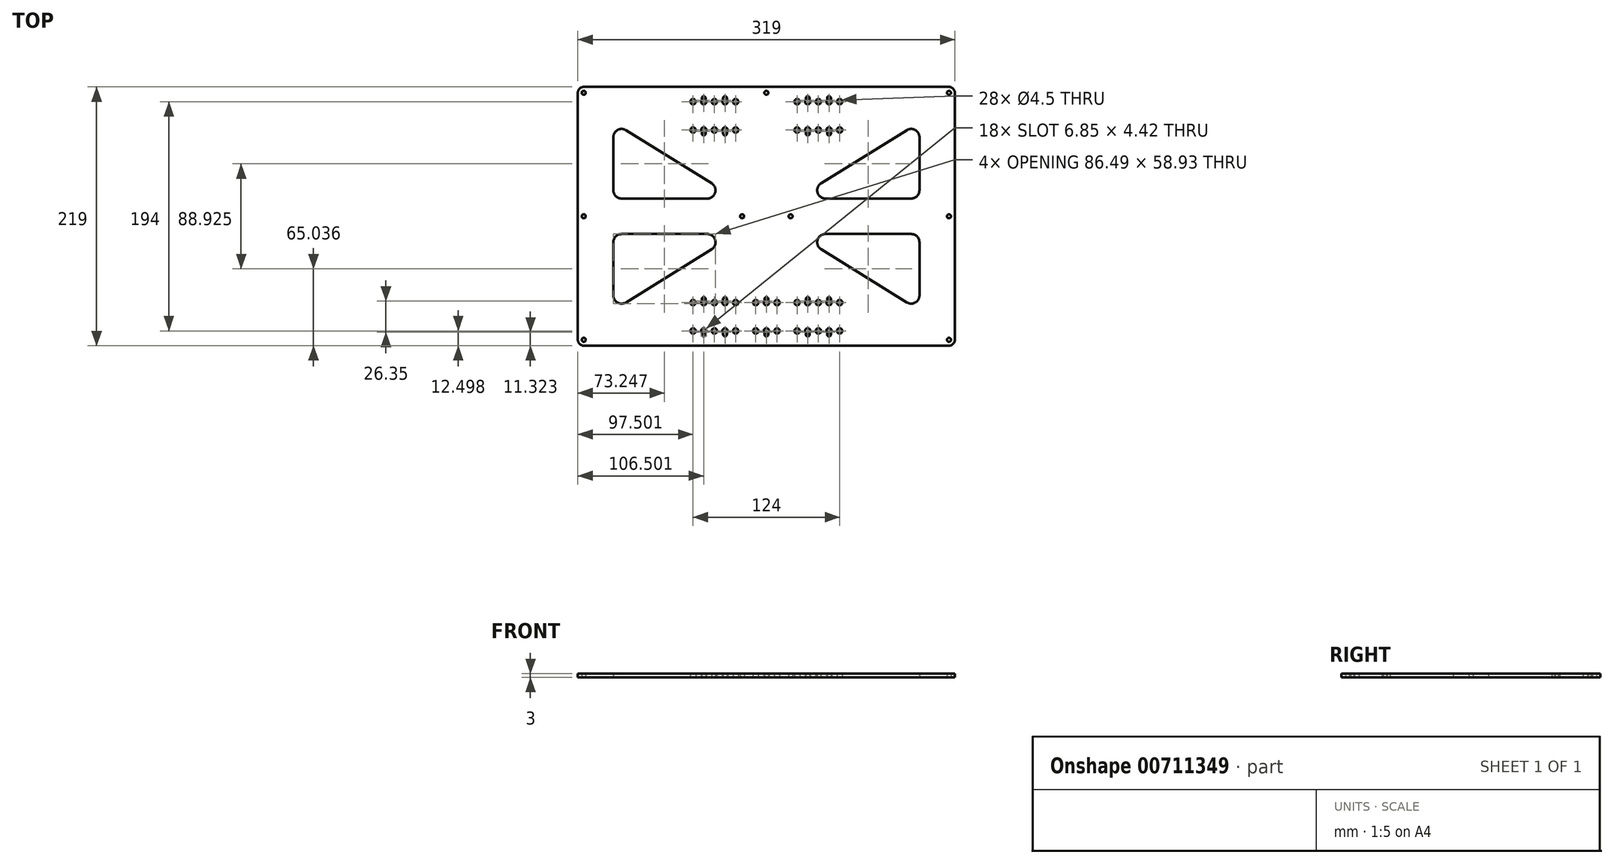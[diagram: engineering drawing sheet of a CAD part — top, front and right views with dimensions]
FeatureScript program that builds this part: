
annotation { "Feature Type Name" : "Feature", "Feature Type Description" : "" }
export const myFeature = defineFeature(function(context is Context, id is Id, definition is map)
    precondition{}
    {
        {
            var Q0;
            Q0=qCreatedBy(makeId("Top.planeOp"),FACE);
            var sketch = newSketch(context, id + "F0", { "sketchPlane" : qUnion([Q0])});
            skLineSegment(sketch, "E0", {"start": v(276.47, 208.94) * mm, "end": v(276.47, 207.52) * mm});
            skArc(sketch, "E1", {"start": v(276.47, 208.94) * mm, "mid": v(274.87, 212.77) * mm, "end": v(273.27, 208.94) * mm});
            skLineSegment(sketch, "E2", {"start": v(273.27, 207.52) * mm, "end": v(273.27, 208.94) * mm});
            skArc(sketch, "E3", {"start": v(273.27, 207.52) * mm, "mid": v(274.87, 205.92) * mm, "end": v(276.47, 207.52) * mm});
            skLineSegment(sketch, "E4", {"start": v(273.27, 236.1) * mm, "end": v(273.27, 237.52) * mm});
            skArc(sketch, "E5", {"start": v(273.27, 236.1) * mm, "mid": v(274.87, 232.27) * mm, "end": v(276.47, 236.1) * mm});
            skLineSegment(sketch, "E6", {"start": v(276.47, 237.52) * mm, "end": v(276.47, 236.1) * mm});
            skArc(sketch, "E7", {"start": v(276.47, 237.52) * mm, "mid": v(274.87, 239.12) * mm, "end": v(273.27, 237.52) * mm});
            skLineSegment(sketch, "E8", {"start": v(170.47, 208.94) * mm, "end": v(170.47, 207.52) * mm});
            skArc(sketch, "E9", {"start": v(170.47, 208.94) * mm, "mid": v(168.87, 212.77) * mm, "end": v(167.27, 208.94) * mm});
            skLineSegment(sketch, "E10", {"start": v(167.27, 207.52) * mm, "end": v(167.27, 208.94) * mm});
            skArc(sketch, "E11", {"start": v(167.27, 207.52) * mm, "mid": v(168.87, 205.92) * mm, "end": v(170.47, 207.52) * mm});
            skLineSegment(sketch, "E12", {"start": v(167.27, 236.1) * mm, "end": v(167.27, 237.52) * mm});
            skArc(sketch, "E13", {"start": v(167.27, 236.1) * mm, "mid": v(168.87, 232.27) * mm, "end": v(170.47, 236.1) * mm});
            skLineSegment(sketch, "E14", {"start": v(170.47, 237.52) * mm, "end": v(170.47, 236.1) * mm});
            skArc(sketch, "E15", {"start": v(170.47, 237.52) * mm, "mid": v(168.87, 239.12) * mm, "end": v(167.27, 237.52) * mm});
            skLineSegment(sketch, "E16", {"start": v(258.47, 208.94) * mm, "end": v(258.47, 207.52) * mm});
            skArc(sketch, "E17", {"start": v(258.47, 208.94) * mm, "mid": v(256.87, 212.77) * mm, "end": v(255.27, 208.94) * mm});
            skLineSegment(sketch, "E18", {"start": v(255.27, 207.52) * mm, "end": v(255.27, 208.94) * mm});
            skArc(sketch, "E19", {"start": v(255.27, 207.52) * mm, "mid": v(256.87, 205.92) * mm, "end": v(258.47, 207.52) * mm});
            skLineSegment(sketch, "E20", {"start": v(255.27, 236.1) * mm, "end": v(255.27, 237.52) * mm});
            skArc(sketch, "E21", {"start": v(255.27, 236.1) * mm, "mid": v(256.87, 232.27) * mm, "end": v(258.47, 236.1) * mm});
            skLineSegment(sketch, "E22", {"start": v(258.47, 237.52) * mm, "end": v(258.47, 236.1) * mm});
            skArc(sketch, "E23", {"start": v(258.47, 237.52) * mm, "mid": v(256.87, 239.12) * mm, "end": v(255.27, 237.52) * mm});
            skLineSegment(sketch, "E24", {"start": v(188.47, 208.94) * mm, "end": v(188.47, 207.52) * mm});
            skArc(sketch, "E25", {"start": v(188.47, 208.94) * mm, "mid": v(186.87, 212.77) * mm, "end": v(185.27, 208.94) * mm});
            skLineSegment(sketch, "E26", {"start": v(185.27, 207.52) * mm, "end": v(185.27, 208.94) * mm});
            skArc(sketch, "E27", {"start": v(185.27, 207.52) * mm, "mid": v(186.87, 205.92) * mm, "end": v(188.47, 207.52) * mm});
            skLineSegment(sketch, "E28", {"start": v(185.27, 236.1) * mm, "end": v(185.27, 237.52) * mm});
            skArc(sketch, "E29", {"start": v(185.27, 236.1) * mm, "mid": v(186.87, 232.27) * mm, "end": v(188.47, 236.1) * mm});
            skLineSegment(sketch, "E30", {"start": v(188.47, 237.52) * mm, "end": v(188.47, 236.1) * mm});
            skArc(sketch, "E31", {"start": v(188.47, 237.52) * mm, "mid": v(186.87, 239.12) * mm, "end": v(185.27, 237.52) * mm});
            skArc(sketch, "E32", {"start": v(62.37, 33.02) * mm, "mid": v(63.84, 29.48) * mm, "end": v(67.37, 28.02) * mm});
            skLineSegment(sketch, "E33", {"start": v(62.37, 242.02) * mm, "end": v(62.37, 33.02) * mm});
            skArc(sketch, "E34", {"start": v(67.37, 247.02) * mm, "mid": v(63.84, 245.55) * mm, "end": v(62.37, 242.02) * mm});
            skLineSegment(sketch, "E35", {"start": v(376.37, 247.02) * mm, "end": v(67.37, 247.02) * mm});
            skArc(sketch, "E36", {"start": v(381.37, 242.02) * mm, "mid": v(379.9, 245.55) * mm, "end": v(376.37, 247.02) * mm});
            skLineSegment(sketch, "E37", {"start": v(381.37, 33.02) * mm, "end": v(381.37, 242.02) * mm});
            skArc(sketch, "E38", {"start": v(376.37, 28.02) * mm, "mid": v(379.9, 29.48) * mm, "end": v(381.37, 33.02) * mm});
            skLineSegment(sketch, "E39", {"start": v(67.37, 28.02) * mm, "end": v(376.37, 28.02) * mm});
            skCircle(sketch, "E40", {"center": v(221.87, 242.02) * mm, "radius": 1.7 * mm});
            skCircle(sketch, "E41", {"center": v(376.37, 242.02) * mm, "radius": 1.7 * mm});
            skCircle(sketch, "E42", {"center": v(376.37, 137.52) * mm, "radius": 1.7 * mm});
            skCircle(sketch, "E43", {"center": v(67.37, 242.02) * mm, "radius": 1.7 * mm});
            skCircle(sketch, "E44", {"center": v(67.37, 137.52) * mm, "radius": 1.7 * mm});
            skCircle(sketch, "E45", {"center": v(67.37, 33.02) * mm, "radius": 1.7 * mm});
            skCircle(sketch, "E46", {"center": v(230.87, 40.52) * mm, "radius": 2.25 * mm});
            skCircle(sketch, "E47", {"center": v(230.87, 64.52) * mm, "radius": 2.25 * mm});
            skCircle(sketch, "E48", {"center": v(212.87, 64.52) * mm, "radius": 2.25 * mm});
            skCircle(sketch, "E49", {"center": v(212.87, 40.52) * mm, "radius": 2.25 * mm});
            skArc(sketch, "E50", {"start": v(220.27, 37.52) * mm, "mid": v(221.87, 35.92) * mm, "end": v(223.47, 37.52) * mm});
            skLineSegment(sketch, "E51", {"start": v(223.47, 37.52) * mm, "end": v(223.47, 38.94) * mm});
            skArc(sketch, "E52", {"start": v(223.47, 38.94) * mm, "mid": v(221.87, 42.77) * mm, "end": v(220.27, 38.94) * mm});
            skLineSegment(sketch, "E53", {"start": v(220.27, 38.94) * mm, "end": v(220.27, 37.52) * mm});
            skArc(sketch, "E54", {"start": v(223.47, 67.52) * mm, "mid": v(221.87, 69.12) * mm, "end": v(220.27, 67.52) * mm});
            skLineSegment(sketch, "E55", {"start": v(220.27, 67.52) * mm, "end": v(220.27, 66.1) * mm});
            skArc(sketch, "E56", {"start": v(220.27, 66.1) * mm, "mid": v(221.87, 62.27) * mm, "end": v(223.47, 66.1) * mm});
            skLineSegment(sketch, "E57", {"start": v(223.47, 66.1) * mm, "end": v(223.47, 67.52) * mm});
            skCircle(sketch, "E58", {"center": v(195.87, 40.52) * mm, "radius": 2.25 * mm});
            skCircle(sketch, "E59", {"center": v(195.87, 64.52) * mm, "radius": 2.25 * mm});
            skCircle(sketch, "E60", {"center": v(177.87, 64.52) * mm, "radius": 2.25 * mm});
            skCircle(sketch, "E61", {"center": v(177.87, 40.52) * mm, "radius": 2.25 * mm});
            skCircle(sketch, "E62", {"center": v(265.87, 40.52) * mm, "radius": 2.25 * mm});
            skCircle(sketch, "E63", {"center": v(265.87, 64.52) * mm, "radius": 2.25 * mm});
            skCircle(sketch, "E64", {"center": v(247.87, 64.52) * mm, "radius": 2.25 * mm});
            skCircle(sketch, "E65", {"center": v(247.87, 40.52) * mm, "radius": 2.25 * mm});
            skCircle(sketch, "E66", {"center": v(159.87, 64.52) * mm, "radius": 2.25 * mm});
            skCircle(sketch, "E67", {"center": v(159.87, 40.52) * mm, "radius": 2.25 * mm});
            skCircle(sketch, "E68", {"center": v(283.87, 40.52) * mm, "radius": 2.25 * mm});
            skCircle(sketch, "E69", {"center": v(283.87, 64.52) * mm, "radius": 2.25 * mm});
            skArc(sketch, "E70", {"start": v(185.27, 37.52) * mm, "mid": v(186.87, 35.92) * mm, "end": v(188.47, 37.52) * mm});
            skLineSegment(sketch, "E71", {"start": v(188.47, 37.52) * mm, "end": v(188.47, 38.94) * mm});
            skArc(sketch, "E72", {"start": v(188.47, 38.94) * mm, "mid": v(186.87, 42.77) * mm, "end": v(185.27, 38.94) * mm});
            skLineSegment(sketch, "E73", {"start": v(185.27, 38.94) * mm, "end": v(185.27, 37.52) * mm});
            skArc(sketch, "E74", {"start": v(188.47, 67.52) * mm, "mid": v(186.87, 69.12) * mm, "end": v(185.27, 67.52) * mm});
            skLineSegment(sketch, "E75", {"start": v(185.27, 67.52) * mm, "end": v(185.27, 66.1) * mm});
            skArc(sketch, "E76", {"start": v(185.27, 66.1) * mm, "mid": v(186.87, 62.27) * mm, "end": v(188.47, 66.1) * mm});
            skLineSegment(sketch, "E77", {"start": v(188.47, 66.1) * mm, "end": v(188.47, 67.52) * mm});
            skArc(sketch, "E78", {"start": v(255.27, 37.52) * mm, "mid": v(256.87, 35.92) * mm, "end": v(258.47, 37.52) * mm});
            skLineSegment(sketch, "E79", {"start": v(258.47, 37.52) * mm, "end": v(258.47, 38.94) * mm});
            skArc(sketch, "E80", {"start": v(258.47, 38.94) * mm, "mid": v(256.87, 42.77) * mm, "end": v(255.27, 38.94) * mm});
            skLineSegment(sketch, "E81", {"start": v(255.27, 38.94) * mm, "end": v(255.27, 37.52) * mm});
            skArc(sketch, "E82", {"start": v(258.47, 67.52) * mm, "mid": v(256.87, 69.12) * mm, "end": v(255.27, 67.52) * mm});
            skLineSegment(sketch, "E83", {"start": v(255.27, 67.52) * mm, "end": v(255.27, 66.1) * mm});
            skArc(sketch, "E84", {"start": v(255.27, 66.1) * mm, "mid": v(256.87, 62.27) * mm, "end": v(258.47, 66.1) * mm});
            skLineSegment(sketch, "E85", {"start": v(258.47, 66.1) * mm, "end": v(258.47, 67.52) * mm});
            skArc(sketch, "E86", {"start": v(167.27, 37.52) * mm, "mid": v(168.87, 35.92) * mm, "end": v(170.47, 37.52) * mm});
            skLineSegment(sketch, "E87", {"start": v(170.47, 37.52) * mm, "end": v(170.47, 38.94) * mm});
            skArc(sketch, "E88", {"start": v(170.47, 38.94) * mm, "mid": v(168.87, 42.77) * mm, "end": v(167.27, 38.94) * mm});
            skLineSegment(sketch, "E89", {"start": v(167.27, 38.94) * mm, "end": v(167.27, 37.52) * mm});
            skArc(sketch, "E90", {"start": v(170.47, 67.52) * mm, "mid": v(168.87, 69.12) * mm, "end": v(167.27, 67.52) * mm});
            skLineSegment(sketch, "E91", {"start": v(167.27, 67.52) * mm, "end": v(167.27, 66.1) * mm});
            skArc(sketch, "E92", {"start": v(167.27, 66.1) * mm, "mid": v(168.87, 62.27) * mm, "end": v(170.47, 66.1) * mm});
            skLineSegment(sketch, "E93", {"start": v(170.47, 66.1) * mm, "end": v(170.47, 67.52) * mm});
            skArc(sketch, "E94", {"start": v(273.27, 37.52) * mm, "mid": v(274.87, 35.92) * mm, "end": v(276.47, 37.52) * mm});
            skLineSegment(sketch, "E95", {"start": v(276.47, 37.52) * mm, "end": v(276.47, 38.94) * mm});
            skArc(sketch, "E96", {"start": v(276.47, 38.94) * mm, "mid": v(274.87, 42.77) * mm, "end": v(273.27, 38.94) * mm});
            skLineSegment(sketch, "E97", {"start": v(273.27, 38.94) * mm, "end": v(273.27, 37.52) * mm});
            skArc(sketch, "E98", {"start": v(276.47, 67.52) * mm, "mid": v(274.87, 69.12) * mm, "end": v(273.27, 67.52) * mm});
            skLineSegment(sketch, "E99", {"start": v(273.27, 67.52) * mm, "end": v(273.27, 66.1) * mm});
            skArc(sketch, "E100", {"start": v(273.27, 66.1) * mm, "mid": v(274.87, 62.27) * mm, "end": v(276.47, 66.1) * mm});
            skLineSegment(sketch, "E101", {"start": v(276.47, 66.1) * mm, "end": v(276.47, 67.52) * mm});
            skLineSegment(sketch, "E102", {"start": v(171.87, 122.52) * mm, "end": v(99.37, 122.52) * mm});
            skArc(sketch, "E103", {"start": v(99.37, 122.52) * mm, "mid": v(94.42, 120.47) * mm, "end": v(92.37, 115.52) * mm});
            skLineSegment(sketch, "E104", {"start": v(92.37, 115.52) * mm, "end": v(92.37, 70.6) * mm});
            skArc(sketch, "E105", {"start": v(92.37, 70.6) * mm, "mid": v(95.97, 64.48) * mm, "end": v(103.06, 64.64) * mm});
            skLineSegment(sketch, "E106", {"start": v(103.06, 64.64) * mm, "end": v(175.56, 109.57) * mm});
            skArc(sketch, "E107", {"start": v(175.56, 109.57) * mm, "mid": v(178.6, 117.44) * mm, "end": v(171.87, 122.52) * mm});
            skLineSegment(sketch, "E108", {"start": v(92.37, 204.45) * mm, "end": v(92.37, 159.52) * mm});
            skArc(sketch, "E109", {"start": v(92.37, 159.52) * mm, "mid": v(94.42, 154.57) * mm, "end": v(99.37, 152.52) * mm});
            skLineSegment(sketch, "E110", {"start": v(99.37, 152.52) * mm, "end": v(171.87, 152.52) * mm});
            skArc(sketch, "E111", {"start": v(171.87, 152.52) * mm, "mid": v(178.6, 157.6) * mm, "end": v(175.56, 165.47) * mm});
            skLineSegment(sketch, "E112", {"start": v(175.56, 165.47) * mm, "end": v(103.06, 210.4) * mm});
            skArc(sketch, "E113", {"start": v(103.06, 210.4) * mm, "mid": v(95.97, 210.56) * mm, "end": v(92.37, 204.45) * mm});
            skLineSegment(sketch, "E114", {"start": v(271.87, 152.52) * mm, "end": v(344.37, 152.52) * mm});
            skArc(sketch, "E115", {"start": v(344.37, 152.52) * mm, "mid": v(349.32, 154.57) * mm, "end": v(351.37, 159.52) * mm});
            skLineSegment(sketch, "E116", {"start": v(351.37, 159.52) * mm, "end": v(351.37, 204.45) * mm});
            skArc(sketch, "E117", {"start": v(351.37, 204.45) * mm, "mid": v(347.78, 210.56) * mm, "end": v(340.68, 210.4) * mm});
            skLineSegment(sketch, "E118", {"start": v(340.68, 210.4) * mm, "end": v(268.18, 165.47) * mm});
            skArc(sketch, "E119", {"start": v(268.18, 165.47) * mm, "mid": v(265.14, 157.6) * mm, "end": v(271.87, 152.52) * mm});
            skLineSegment(sketch, "E120", {"start": v(351.37, 70.6) * mm, "end": v(351.37, 115.52) * mm});
            skArc(sketch, "E121", {"start": v(351.37, 115.52) * mm, "mid": v(349.32, 120.47) * mm, "end": v(344.37, 122.52) * mm});
            skLineSegment(sketch, "E122", {"start": v(344.37, 122.52) * mm, "end": v(271.87, 122.52) * mm});
            skArc(sketch, "E123", {"start": v(271.87, 122.52) * mm, "mid": v(265.14, 117.44) * mm, "end": v(268.18, 109.57) * mm});
            skLineSegment(sketch, "E124", {"start": v(268.18, 109.57) * mm, "end": v(340.68, 64.64) * mm});
            skArc(sketch, "E125", {"start": v(340.68, 64.64) * mm, "mid": v(347.78, 64.48) * mm, "end": v(351.37, 70.6) * mm});
            skCircle(sketch, "E126", {"center": v(242.37, 137.52) * mm, "radius": 1.7 * mm});
            skCircle(sketch, "E127", {"center": v(201.37, 137.52) * mm, "radius": 1.7 * mm});
            skCircle(sketch, "E128", {"center": v(195.87, 234.52) * mm, "radius": 2.25 * mm});
            skCircle(sketch, "E129", {"center": v(195.87, 210.52) * mm, "radius": 2.25 * mm});
            skCircle(sketch, "E130", {"center": v(177.87, 210.52) * mm, "radius": 2.25 * mm});
            skCircle(sketch, "E131", {"center": v(177.87, 234.52) * mm, "radius": 2.25 * mm});
            skCircle(sketch, "E132", {"center": v(265.87, 234.52) * mm, "radius": 2.25 * mm});
            skCircle(sketch, "E133", {"center": v(265.87, 210.52) * mm, "radius": 2.25 * mm});
            skCircle(sketch, "E134", {"center": v(247.87, 210.52) * mm, "radius": 2.25 * mm});
            skCircle(sketch, "E135", {"center": v(247.87, 234.52) * mm, "radius": 2.25 * mm});
            skCircle(sketch, "E136", {"center": v(159.87, 210.52) * mm, "radius": 2.25 * mm});
            skCircle(sketch, "E137", {"center": v(159.87, 234.52) * mm, "radius": 2.25 * mm});
            skCircle(sketch, "E138", {"center": v(283.87, 234.52) * mm, "radius": 2.25 * mm});
            skCircle(sketch, "E139", {"center": v(283.87, 210.52) * mm, "radius": 2.25 * mm});
            skCircle(sketch, "E140", {"center": v(376.37, 33.02) * mm, "radius": 1.7 * mm});
            skLineSegment(sketch, "E141", {"start": v(221.87, 242.02) * mm, "end": v(219.33, 242.02) * mm});
            skLineSegment(sketch, "E142", {"start": v(221.87, 242.02) * mm, "end": v(221.87, 239.48) * mm});
            skLineSegment(sketch, "E143", {"start": v(221.87, 242.02) * mm, "end": v(224.41, 242.02) * mm});
            skLineSegment(sketch, "E144", {"start": v(221.87, 242.02) * mm, "end": v(221.87, 244.56) * mm});
            skLineSegment(sketch, "E145", {"start": v(219.33, 242.02) * mm, "end": v(217.63, 242.02) * mm});
            skLineSegment(sketch, "E146", {"start": v(221.87, 239.48) * mm, "end": v(221.87, 237.78) * mm});
            skLineSegment(sketch, "E147", {"start": v(224.41, 242.02) * mm, "end": v(226.11, 242.02) * mm});
            skLineSegment(sketch, "E148", {"start": v(221.87, 244.56) * mm, "end": v(221.87, 246.26) * mm});
            skLineSegment(sketch, "E149", {"start": v(376.37, 242.02) * mm, "end": v(373.83, 242.02) * mm});
            skLineSegment(sketch, "E150", {"start": v(376.37, 242.02) * mm, "end": v(376.37, 239.48) * mm});
            skLineSegment(sketch, "E151", {"start": v(376.37, 242.02) * mm, "end": v(378.91, 242.02) * mm});
            skLineSegment(sketch, "E152", {"start": v(376.37, 242.02) * mm, "end": v(376.37, 244.56) * mm});
            skLineSegment(sketch, "E153", {"start": v(373.83, 242.02) * mm, "end": v(372.13, 242.02) * mm});
            skLineSegment(sketch, "E154", {"start": v(376.37, 239.48) * mm, "end": v(376.37, 237.78) * mm});
            skLineSegment(sketch, "E155", {"start": v(378.91, 242.02) * mm, "end": v(380.61, 242.02) * mm});
            skLineSegment(sketch, "E156", {"start": v(376.37, 244.56) * mm, "end": v(376.37, 246.26) * mm});
            skLineSegment(sketch, "E157", {"start": v(376.37, 137.52) * mm, "end": v(373.83, 137.52) * mm});
            skLineSegment(sketch, "E158", {"start": v(376.37, 137.52) * mm, "end": v(376.37, 134.98) * mm});
            skLineSegment(sketch, "E159", {"start": v(376.37, 137.52) * mm, "end": v(378.91, 137.52) * mm});
            skLineSegment(sketch, "E160", {"start": v(376.37, 137.52) * mm, "end": v(376.37, 140.06) * mm});
            skLineSegment(sketch, "E161", {"start": v(373.83, 137.52) * mm, "end": v(372.13, 137.52) * mm});
            skLineSegment(sketch, "E162", {"start": v(376.37, 134.98) * mm, "end": v(376.37, 133.28) * mm});
            skLineSegment(sketch, "E163", {"start": v(378.91, 137.52) * mm, "end": v(380.61, 137.52) * mm});
            skLineSegment(sketch, "E164", {"start": v(376.37, 140.06) * mm, "end": v(376.37, 141.76) * mm});
            skLineSegment(sketch, "E165", {"start": v(376.37, 33.02) * mm, "end": v(373.83, 33.02) * mm});
            skLineSegment(sketch, "E166", {"start": v(376.37, 33.02) * mm, "end": v(376.37, 30.48) * mm});
            skLineSegment(sketch, "E167", {"start": v(376.37, 33.02) * mm, "end": v(378.91, 33.02) * mm});
            skLineSegment(sketch, "E168", {"start": v(376.37, 33.02) * mm, "end": v(376.37, 35.56) * mm});
            skLineSegment(sketch, "E169", {"start": v(373.83, 33.02) * mm, "end": v(372.13, 33.02) * mm});
            skLineSegment(sketch, "E170", {"start": v(376.37, 30.48) * mm, "end": v(376.37, 28.78) * mm});
            skLineSegment(sketch, "E171", {"start": v(378.91, 33.02) * mm, "end": v(380.61, 33.02) * mm});
            skLineSegment(sketch, "E172", {"start": v(376.37, 35.56) * mm, "end": v(376.37, 37.26) * mm});
            skLineSegment(sketch, "E173", {"start": v(67.37, 242.02) * mm, "end": v(64.83, 242.02) * mm});
            skLineSegment(sketch, "E174", {"start": v(67.37, 242.02) * mm, "end": v(67.37, 239.48) * mm});
            skLineSegment(sketch, "E175", {"start": v(67.37, 242.02) * mm, "end": v(69.91, 242.02) * mm});
            skLineSegment(sketch, "E176", {"start": v(67.37, 242.02) * mm, "end": v(67.37, 244.56) * mm});
            skLineSegment(sketch, "E177", {"start": v(64.83, 242.02) * mm, "end": v(63.13, 242.02) * mm});
            skLineSegment(sketch, "E178", {"start": v(67.37, 239.48) * mm, "end": v(67.37, 237.78) * mm});
            skLineSegment(sketch, "E179", {"start": v(69.91, 242.02) * mm, "end": v(71.61, 242.02) * mm});
            skLineSegment(sketch, "E180", {"start": v(67.37, 244.56) * mm, "end": v(67.37, 246.26) * mm});
            skLineSegment(sketch, "E181", {"start": v(67.37, 137.52) * mm, "end": v(64.83, 137.52) * mm});
            skLineSegment(sketch, "E182", {"start": v(67.37, 137.52) * mm, "end": v(67.37, 134.98) * mm});
            skLineSegment(sketch, "E183", {"start": v(67.37, 137.52) * mm, "end": v(69.91, 137.52) * mm});
            skLineSegment(sketch, "E184", {"start": v(67.37, 137.52) * mm, "end": v(67.37, 140.06) * mm});
            skLineSegment(sketch, "E185", {"start": v(64.83, 137.52) * mm, "end": v(63.13, 137.52) * mm});
            skLineSegment(sketch, "E186", {"start": v(67.37, 134.98) * mm, "end": v(67.37, 133.28) * mm});
            skLineSegment(sketch, "E187", {"start": v(69.91, 137.52) * mm, "end": v(71.61, 137.52) * mm});
            skLineSegment(sketch, "E188", {"start": v(67.37, 140.06) * mm, "end": v(67.37, 141.76) * mm});
            skLineSegment(sketch, "E189", {"start": v(67.37, 33.02) * mm, "end": v(64.83, 33.02) * mm});
            skLineSegment(sketch, "E190", {"start": v(67.37, 33.02) * mm, "end": v(67.37, 30.48) * mm});
            skLineSegment(sketch, "E191", {"start": v(67.37, 33.02) * mm, "end": v(69.91, 33.02) * mm});
            skLineSegment(sketch, "E192", {"start": v(67.37, 33.02) * mm, "end": v(67.37, 35.56) * mm});
            skLineSegment(sketch, "E193", {"start": v(64.83, 33.02) * mm, "end": v(63.13, 33.02) * mm});
            skLineSegment(sketch, "E194", {"start": v(67.37, 30.48) * mm, "end": v(67.37, 28.78) * mm});
            skLineSegment(sketch, "E195", {"start": v(69.91, 33.02) * mm, "end": v(71.61, 33.02) * mm});
            skLineSegment(sketch, "E196", {"start": v(67.37, 35.56) * mm, "end": v(67.37, 37.26) * mm});
            skLineSegment(sketch, "E197", {"start": v(230.87, 40.52) * mm, "end": v(228.33, 40.52) * mm});
            skLineSegment(sketch, "E198", {"start": v(230.87, 40.52) * mm, "end": v(230.87, 37.98) * mm});
            skLineSegment(sketch, "E199", {"start": v(230.87, 40.52) * mm, "end": v(233.41, 40.52) * mm});
            skLineSegment(sketch, "E200", {"start": v(230.87, 40.52) * mm, "end": v(230.87, 43.06) * mm});
            skLineSegment(sketch, "E201", {"start": v(228.33, 40.52) * mm, "end": v(226.08, 40.52) * mm});
            skLineSegment(sketch, "E202", {"start": v(230.87, 37.98) * mm, "end": v(230.87, 35.73) * mm});
            skLineSegment(sketch, "E203", {"start": v(233.41, 40.52) * mm, "end": v(235.66, 40.52) * mm});
            skLineSegment(sketch, "E204", {"start": v(230.87, 43.06) * mm, "end": v(230.87, 45.3) * mm});
            skLineSegment(sketch, "E205", {"start": v(230.87, 64.52) * mm, "end": v(228.33, 64.52) * mm});
            skLineSegment(sketch, "E206", {"start": v(230.87, 64.52) * mm, "end": v(230.87, 61.98) * mm});
            skLineSegment(sketch, "E207", {"start": v(230.87, 64.52) * mm, "end": v(233.41, 64.52) * mm});
            skLineSegment(sketch, "E208", {"start": v(230.87, 64.52) * mm, "end": v(230.87, 67.06) * mm});
            skLineSegment(sketch, "E209", {"start": v(228.33, 64.52) * mm, "end": v(226.08, 64.52) * mm});
            skLineSegment(sketch, "E210", {"start": v(230.87, 61.98) * mm, "end": v(230.87, 59.73) * mm});
            skLineSegment(sketch, "E211", {"start": v(233.41, 64.52) * mm, "end": v(235.66, 64.52) * mm});
            skLineSegment(sketch, "E212", {"start": v(230.87, 67.06) * mm, "end": v(230.87, 69.3) * mm});
            skLineSegment(sketch, "E213", {"start": v(212.87, 64.52) * mm, "end": v(210.33, 64.52) * mm});
            skLineSegment(sketch, "E214", {"start": v(212.87, 64.52) * mm, "end": v(212.87, 61.98) * mm});
            skLineSegment(sketch, "E215", {"start": v(212.87, 64.52) * mm, "end": v(215.41, 64.52) * mm});
            skLineSegment(sketch, "E216", {"start": v(212.87, 64.52) * mm, "end": v(212.87, 67.06) * mm});
            skLineSegment(sketch, "E217", {"start": v(210.33, 64.52) * mm, "end": v(208.08, 64.52) * mm});
            skLineSegment(sketch, "E218", {"start": v(212.87, 61.98) * mm, "end": v(212.87, 59.73) * mm});
            skLineSegment(sketch, "E219", {"start": v(215.41, 64.52) * mm, "end": v(217.66, 64.52) * mm});
            skLineSegment(sketch, "E220", {"start": v(212.87, 67.06) * mm, "end": v(212.87, 69.3) * mm});
            skLineSegment(sketch, "E221", {"start": v(212.87, 40.52) * mm, "end": v(210.33, 40.52) * mm});
            skLineSegment(sketch, "E222", {"start": v(212.87, 40.52) * mm, "end": v(212.87, 37.98) * mm});
            skLineSegment(sketch, "E223", {"start": v(212.87, 40.52) * mm, "end": v(215.41, 40.52) * mm});
            skLineSegment(sketch, "E224", {"start": v(212.87, 40.52) * mm, "end": v(212.87, 43.06) * mm});
            skLineSegment(sketch, "E225", {"start": v(210.33, 40.52) * mm, "end": v(208.08, 40.52) * mm});
            skLineSegment(sketch, "E226", {"start": v(212.87, 37.98) * mm, "end": v(212.87, 35.73) * mm});
            skLineSegment(sketch, "E227", {"start": v(215.41, 40.52) * mm, "end": v(217.66, 40.52) * mm});
            skLineSegment(sketch, "E228", {"start": v(212.87, 43.06) * mm, "end": v(212.87, 45.3) * mm});
            skLineSegment(sketch, "E229", {"start": v(195.87, 40.52) * mm, "end": v(193.33, 40.52) * mm});
            skLineSegment(sketch, "E230", {"start": v(195.87, 40.52) * mm, "end": v(195.87, 37.98) * mm});
            skLineSegment(sketch, "E231", {"start": v(195.87, 40.52) * mm, "end": v(198.41, 40.52) * mm});
            skLineSegment(sketch, "E232", {"start": v(195.87, 40.52) * mm, "end": v(195.87, 43.06) * mm});
            skLineSegment(sketch, "E233", {"start": v(193.33, 40.52) * mm, "end": v(191.08, 40.52) * mm});
            skLineSegment(sketch, "E234", {"start": v(195.87, 37.98) * mm, "end": v(195.87, 35.73) * mm});
            skLineSegment(sketch, "E235", {"start": v(198.41, 40.52) * mm, "end": v(200.66, 40.52) * mm});
            skLineSegment(sketch, "E236", {"start": v(195.87, 43.06) * mm, "end": v(195.87, 45.3) * mm});
            skLineSegment(sketch, "E237", {"start": v(195.87, 64.52) * mm, "end": v(193.33, 64.52) * mm});
            skLineSegment(sketch, "E238", {"start": v(195.87, 64.52) * mm, "end": v(195.87, 61.98) * mm});
            skLineSegment(sketch, "E239", {"start": v(195.87, 64.52) * mm, "end": v(198.41, 64.52) * mm});
            skLineSegment(sketch, "E240", {"start": v(195.87, 64.52) * mm, "end": v(195.87, 67.06) * mm});
            skLineSegment(sketch, "E241", {"start": v(193.33, 64.52) * mm, "end": v(191.08, 64.52) * mm});
            skLineSegment(sketch, "E242", {"start": v(195.87, 61.98) * mm, "end": v(195.87, 59.73) * mm});
            skLineSegment(sketch, "E243", {"start": v(198.41, 64.52) * mm, "end": v(200.66, 64.52) * mm});
            skLineSegment(sketch, "E244", {"start": v(195.87, 67.06) * mm, "end": v(195.87, 69.3) * mm});
            skLineSegment(sketch, "E245", {"start": v(177.87, 64.52) * mm, "end": v(175.33, 64.52) * mm});
            skLineSegment(sketch, "E246", {"start": v(177.87, 64.52) * mm, "end": v(177.87, 61.98) * mm});
            skLineSegment(sketch, "E247", {"start": v(177.87, 64.52) * mm, "end": v(180.41, 64.52) * mm});
            skLineSegment(sketch, "E248", {"start": v(177.87, 64.52) * mm, "end": v(177.87, 67.06) * mm});
            skLineSegment(sketch, "E249", {"start": v(175.33, 64.52) * mm, "end": v(173.08, 64.52) * mm});
            skLineSegment(sketch, "E250", {"start": v(177.87, 61.98) * mm, "end": v(177.87, 59.73) * mm});
            skLineSegment(sketch, "E251", {"start": v(180.41, 64.52) * mm, "end": v(182.66, 64.52) * mm});
            skLineSegment(sketch, "E252", {"start": v(177.87, 67.06) * mm, "end": v(177.87, 69.3) * mm});
            skLineSegment(sketch, "E253", {"start": v(177.87, 40.52) * mm, "end": v(175.33, 40.52) * mm});
            skLineSegment(sketch, "E254", {"start": v(177.87, 40.52) * mm, "end": v(177.87, 37.98) * mm});
            skLineSegment(sketch, "E255", {"start": v(177.87, 40.52) * mm, "end": v(180.41, 40.52) * mm});
            skLineSegment(sketch, "E256", {"start": v(177.87, 40.52) * mm, "end": v(177.87, 43.06) * mm});
            skLineSegment(sketch, "E257", {"start": v(175.33, 40.52) * mm, "end": v(173.08, 40.52) * mm});
            skLineSegment(sketch, "E258", {"start": v(177.87, 37.98) * mm, "end": v(177.87, 35.73) * mm});
            skLineSegment(sketch, "E259", {"start": v(180.41, 40.52) * mm, "end": v(182.66, 40.52) * mm});
            skLineSegment(sketch, "E260", {"start": v(177.87, 43.06) * mm, "end": v(177.87, 45.3) * mm});
            skLineSegment(sketch, "E261", {"start": v(265.87, 40.52) * mm, "end": v(263.33, 40.52) * mm});
            skLineSegment(sketch, "E262", {"start": v(265.87, 40.52) * mm, "end": v(265.87, 37.98) * mm});
            skLineSegment(sketch, "E263", {"start": v(265.87, 40.52) * mm, "end": v(268.41, 40.52) * mm});
            skLineSegment(sketch, "E264", {"start": v(265.87, 40.52) * mm, "end": v(265.87, 43.06) * mm});
            skLineSegment(sketch, "E265", {"start": v(263.33, 40.52) * mm, "end": v(261.08, 40.52) * mm});
            skLineSegment(sketch, "E266", {"start": v(265.87, 37.98) * mm, "end": v(265.87, 35.73) * mm});
            skLineSegment(sketch, "E267", {"start": v(268.41, 40.52) * mm, "end": v(270.66, 40.52) * mm});
            skLineSegment(sketch, "E268", {"start": v(265.87, 43.06) * mm, "end": v(265.87, 45.3) * mm});
            skLineSegment(sketch, "E269", {"start": v(265.87, 64.52) * mm, "end": v(263.33, 64.52) * mm});
            skLineSegment(sketch, "E270", {"start": v(265.87, 64.52) * mm, "end": v(265.87, 61.98) * mm});
            skLineSegment(sketch, "E271", {"start": v(265.87, 64.52) * mm, "end": v(268.41, 64.52) * mm});
            skLineSegment(sketch, "E272", {"start": v(265.87, 64.52) * mm, "end": v(265.87, 67.06) * mm});
            skLineSegment(sketch, "E273", {"start": v(263.33, 64.52) * mm, "end": v(261.08, 64.52) * mm});
            skLineSegment(sketch, "E274", {"start": v(265.87, 61.98) * mm, "end": v(265.87, 59.73) * mm});
            skLineSegment(sketch, "E275", {"start": v(268.41, 64.52) * mm, "end": v(270.66, 64.52) * mm});
            skLineSegment(sketch, "E276", {"start": v(265.87, 67.06) * mm, "end": v(265.87, 69.3) * mm});
            skLineSegment(sketch, "E277", {"start": v(247.87, 64.52) * mm, "end": v(245.33, 64.52) * mm});
            skLineSegment(sketch, "E278", {"start": v(247.87, 64.52) * mm, "end": v(247.87, 61.98) * mm});
            skLineSegment(sketch, "E279", {"start": v(247.87, 64.52) * mm, "end": v(250.41, 64.52) * mm});
            skLineSegment(sketch, "E280", {"start": v(247.87, 64.52) * mm, "end": v(247.87, 67.06) * mm});
            skLineSegment(sketch, "E281", {"start": v(245.33, 64.52) * mm, "end": v(243.08, 64.52) * mm});
            skLineSegment(sketch, "E282", {"start": v(247.87, 61.98) * mm, "end": v(247.87, 59.73) * mm});
            skLineSegment(sketch, "E283", {"start": v(250.41, 64.52) * mm, "end": v(252.66, 64.52) * mm});
            skLineSegment(sketch, "E284", {"start": v(247.87, 67.06) * mm, "end": v(247.87, 69.3) * mm});
            skLineSegment(sketch, "E285", {"start": v(247.87, 40.52) * mm, "end": v(245.33, 40.52) * mm});
            skLineSegment(sketch, "E286", {"start": v(247.87, 40.52) * mm, "end": v(247.87, 37.98) * mm});
            skLineSegment(sketch, "E287", {"start": v(247.87, 40.52) * mm, "end": v(250.41, 40.52) * mm});
            skLineSegment(sketch, "E288", {"start": v(247.87, 40.52) * mm, "end": v(247.87, 43.06) * mm});
            skLineSegment(sketch, "E289", {"start": v(245.33, 40.52) * mm, "end": v(243.08, 40.52) * mm});
            skLineSegment(sketch, "E290", {"start": v(247.87, 37.98) * mm, "end": v(247.87, 35.73) * mm});
            skLineSegment(sketch, "E291", {"start": v(250.41, 40.52) * mm, "end": v(252.66, 40.52) * mm});
            skLineSegment(sketch, "E292", {"start": v(247.87, 43.06) * mm, "end": v(247.87, 45.3) * mm});
            skLineSegment(sketch, "E293", {"start": v(159.87, 64.52) * mm, "end": v(157.33, 64.52) * mm});
            skLineSegment(sketch, "E294", {"start": v(159.87, 64.52) * mm, "end": v(159.87, 61.98) * mm});
            skLineSegment(sketch, "E295", {"start": v(159.87, 64.52) * mm, "end": v(162.41, 64.52) * mm});
            skLineSegment(sketch, "E296", {"start": v(159.87, 64.52) * mm, "end": v(159.87, 67.06) * mm});
            skLineSegment(sketch, "E297", {"start": v(157.33, 64.52) * mm, "end": v(155.08, 64.52) * mm});
            skLineSegment(sketch, "E298", {"start": v(159.87, 61.98) * mm, "end": v(159.87, 59.73) * mm});
            skLineSegment(sketch, "E299", {"start": v(162.41, 64.52) * mm, "end": v(164.66, 64.52) * mm});
            skLineSegment(sketch, "E300", {"start": v(159.87, 67.06) * mm, "end": v(159.87, 69.3) * mm});
            skLineSegment(sketch, "E301", {"start": v(159.87, 40.52) * mm, "end": v(157.33, 40.52) * mm});
            skLineSegment(sketch, "E302", {"start": v(159.87, 40.52) * mm, "end": v(159.87, 37.98) * mm});
            skLineSegment(sketch, "E303", {"start": v(159.87, 40.52) * mm, "end": v(162.41, 40.52) * mm});
            skLineSegment(sketch, "E304", {"start": v(159.87, 40.52) * mm, "end": v(159.87, 43.06) * mm});
            skLineSegment(sketch, "E305", {"start": v(157.33, 40.52) * mm, "end": v(155.08, 40.52) * mm});
            skLineSegment(sketch, "E306", {"start": v(159.87, 37.98) * mm, "end": v(159.87, 35.73) * mm});
            skLineSegment(sketch, "E307", {"start": v(162.41, 40.52) * mm, "end": v(164.66, 40.52) * mm});
            skLineSegment(sketch, "E308", {"start": v(159.87, 43.06) * mm, "end": v(159.87, 45.3) * mm});
            skLineSegment(sketch, "E309", {"start": v(283.87, 40.52) * mm, "end": v(281.33, 40.52) * mm});
            skLineSegment(sketch, "E310", {"start": v(283.87, 40.52) * mm, "end": v(283.87, 37.98) * mm});
            skLineSegment(sketch, "E311", {"start": v(283.87, 40.52) * mm, "end": v(286.41, 40.52) * mm});
            skLineSegment(sketch, "E312", {"start": v(283.87, 40.52) * mm, "end": v(283.87, 43.06) * mm});
            skLineSegment(sketch, "E313", {"start": v(281.33, 40.52) * mm, "end": v(279.08, 40.52) * mm});
            skLineSegment(sketch, "E314", {"start": v(283.87, 37.98) * mm, "end": v(283.87, 35.73) * mm});
            skLineSegment(sketch, "E315", {"start": v(286.41, 40.52) * mm, "end": v(288.66, 40.52) * mm});
            skLineSegment(sketch, "E316", {"start": v(283.87, 43.06) * mm, "end": v(283.87, 45.3) * mm});
            skLineSegment(sketch, "E317", {"start": v(283.87, 64.52) * mm, "end": v(281.33, 64.52) * mm});
            skLineSegment(sketch, "E318", {"start": v(283.87, 64.52) * mm, "end": v(283.87, 61.98) * mm});
            skLineSegment(sketch, "E319", {"start": v(283.87, 64.52) * mm, "end": v(286.41, 64.52) * mm});
            skLineSegment(sketch, "E320", {"start": v(283.87, 64.52) * mm, "end": v(283.87, 67.06) * mm});
            skLineSegment(sketch, "E321", {"start": v(281.33, 64.52) * mm, "end": v(279.08, 64.52) * mm});
            skLineSegment(sketch, "E322", {"start": v(283.87, 61.98) * mm, "end": v(283.87, 59.73) * mm});
            skLineSegment(sketch, "E323", {"start": v(286.41, 64.52) * mm, "end": v(288.66, 64.52) * mm});
            skLineSegment(sketch, "E324", {"start": v(283.87, 67.06) * mm, "end": v(283.87, 69.3) * mm});
            skLineSegment(sketch, "E325", {"start": v(242.37, 137.52) * mm, "end": v(239.83, 137.52) * mm});
            skLineSegment(sketch, "E326", {"start": v(242.37, 137.52) * mm, "end": v(242.37, 134.98) * mm});
            skLineSegment(sketch, "E327", {"start": v(242.37, 137.52) * mm, "end": v(244.91, 137.52) * mm});
            skLineSegment(sketch, "E328", {"start": v(242.37, 137.52) * mm, "end": v(242.37, 140.06) * mm});
            skLineSegment(sketch, "E329", {"start": v(239.83, 137.52) * mm, "end": v(238.13, 137.52) * mm});
            skLineSegment(sketch, "E330", {"start": v(242.37, 134.98) * mm, "end": v(242.37, 133.28) * mm});
            skLineSegment(sketch, "E331", {"start": v(244.91, 137.52) * mm, "end": v(246.61, 137.52) * mm});
            skLineSegment(sketch, "E332", {"start": v(242.37, 140.06) * mm, "end": v(242.37, 141.76) * mm});
            skLineSegment(sketch, "E333", {"start": v(201.37, 137.52) * mm, "end": v(198.83, 137.52) * mm});
            skLineSegment(sketch, "E334", {"start": v(201.37, 137.52) * mm, "end": v(201.37, 134.98) * mm});
            skLineSegment(sketch, "E335", {"start": v(201.37, 137.52) * mm, "end": v(203.91, 137.52) * mm});
            skLineSegment(sketch, "E336", {"start": v(201.37, 137.52) * mm, "end": v(201.37, 140.06) * mm});
            skLineSegment(sketch, "E337", {"start": v(198.83, 137.52) * mm, "end": v(197.13, 137.52) * mm});
            skLineSegment(sketch, "E338", {"start": v(201.37, 134.98) * mm, "end": v(201.37, 133.28) * mm});
            skLineSegment(sketch, "E339", {"start": v(203.91, 137.52) * mm, "end": v(205.61, 137.52) * mm});
            skLineSegment(sketch, "E340", {"start": v(201.37, 140.06) * mm, "end": v(201.37, 141.76) * mm});
            skLineSegment(sketch, "E341", {"start": v(195.87, 234.52) * mm, "end": v(193.33, 234.52) * mm});
            skLineSegment(sketch, "E342", {"start": v(195.87, 234.52) * mm, "end": v(195.87, 231.98) * mm});
            skLineSegment(sketch, "E343", {"start": v(195.87, 234.52) * mm, "end": v(198.41, 234.52) * mm});
            skLineSegment(sketch, "E344", {"start": v(195.87, 234.52) * mm, "end": v(195.87, 237.06) * mm});
            skLineSegment(sketch, "E345", {"start": v(193.33, 234.52) * mm, "end": v(191.08, 234.52) * mm});
            skLineSegment(sketch, "E346", {"start": v(195.87, 231.98) * mm, "end": v(195.87, 229.73) * mm});
            skLineSegment(sketch, "E347", {"start": v(198.41, 234.52) * mm, "end": v(200.66, 234.52) * mm});
            skLineSegment(sketch, "E348", {"start": v(195.87, 237.06) * mm, "end": v(195.87, 239.3) * mm});
            skLineSegment(sketch, "E349", {"start": v(195.87, 210.52) * mm, "end": v(193.33, 210.52) * mm});
            skLineSegment(sketch, "E350", {"start": v(195.87, 210.52) * mm, "end": v(195.87, 207.98) * mm});
            skLineSegment(sketch, "E351", {"start": v(195.87, 210.52) * mm, "end": v(198.41, 210.52) * mm});
            skLineSegment(sketch, "E352", {"start": v(195.87, 210.52) * mm, "end": v(195.87, 213.06) * mm});
            skLineSegment(sketch, "E353", {"start": v(193.33, 210.52) * mm, "end": v(191.08, 210.52) * mm});
            skLineSegment(sketch, "E354", {"start": v(195.87, 207.98) * mm, "end": v(195.87, 205.73) * mm});
            skLineSegment(sketch, "E355", {"start": v(198.41, 210.52) * mm, "end": v(200.66, 210.52) * mm});
            skLineSegment(sketch, "E356", {"start": v(195.87, 213.06) * mm, "end": v(195.87, 215.3) * mm});
            skLineSegment(sketch, "E357", {"start": v(177.87, 210.52) * mm, "end": v(175.33, 210.52) * mm});
            skLineSegment(sketch, "E358", {"start": v(177.87, 210.52) * mm, "end": v(177.87, 207.98) * mm});
            skLineSegment(sketch, "E359", {"start": v(177.87, 210.52) * mm, "end": v(180.41, 210.52) * mm});
            skLineSegment(sketch, "E360", {"start": v(177.87, 210.52) * mm, "end": v(177.87, 213.06) * mm});
            skLineSegment(sketch, "E361", {"start": v(175.33, 210.52) * mm, "end": v(173.08, 210.52) * mm});
            skLineSegment(sketch, "E362", {"start": v(177.87, 207.98) * mm, "end": v(177.87, 205.73) * mm});
            skLineSegment(sketch, "E363", {"start": v(180.41, 210.52) * mm, "end": v(182.66, 210.52) * mm});
            skLineSegment(sketch, "E364", {"start": v(177.87, 213.06) * mm, "end": v(177.87, 215.3) * mm});
            skLineSegment(sketch, "E365", {"start": v(177.87, 234.52) * mm, "end": v(175.33, 234.52) * mm});
            skLineSegment(sketch, "E366", {"start": v(177.87, 234.52) * mm, "end": v(177.87, 231.98) * mm});
            skLineSegment(sketch, "E367", {"start": v(177.87, 234.52) * mm, "end": v(180.41, 234.52) * mm});
            skLineSegment(sketch, "E368", {"start": v(177.87, 234.52) * mm, "end": v(177.87, 237.06) * mm});
            skLineSegment(sketch, "E369", {"start": v(175.33, 234.52) * mm, "end": v(173.08, 234.52) * mm});
            skLineSegment(sketch, "E370", {"start": v(177.87, 231.98) * mm, "end": v(177.87, 229.73) * mm});
            skLineSegment(sketch, "E371", {"start": v(180.41, 234.52) * mm, "end": v(182.66, 234.52) * mm});
            skLineSegment(sketch, "E372", {"start": v(177.87, 237.06) * mm, "end": v(177.87, 239.3) * mm});
            skLineSegment(sketch, "E373", {"start": v(265.87, 234.52) * mm, "end": v(263.33, 234.52) * mm});
            skLineSegment(sketch, "E374", {"start": v(265.87, 234.52) * mm, "end": v(265.87, 231.98) * mm});
            skLineSegment(sketch, "E375", {"start": v(265.87, 234.52) * mm, "end": v(268.41, 234.52) * mm});
            skLineSegment(sketch, "E376", {"start": v(265.87, 234.52) * mm, "end": v(265.87, 237.06) * mm});
            skLineSegment(sketch, "E377", {"start": v(263.33, 234.52) * mm, "end": v(261.08, 234.52) * mm});
            skLineSegment(sketch, "E378", {"start": v(265.87, 231.98) * mm, "end": v(265.87, 229.73) * mm});
            skLineSegment(sketch, "E379", {"start": v(268.41, 234.52) * mm, "end": v(270.66, 234.52) * mm});
            skLineSegment(sketch, "E380", {"start": v(265.87, 237.06) * mm, "end": v(265.87, 239.3) * mm});
            skLineSegment(sketch, "E381", {"start": v(265.87, 210.52) * mm, "end": v(263.33, 210.52) * mm});
            skLineSegment(sketch, "E382", {"start": v(265.87, 210.52) * mm, "end": v(265.87, 207.98) * mm});
            skLineSegment(sketch, "E383", {"start": v(265.87, 210.52) * mm, "end": v(268.41, 210.52) * mm});
            skLineSegment(sketch, "E384", {"start": v(265.87, 210.52) * mm, "end": v(265.87, 213.06) * mm});
            skLineSegment(sketch, "E385", {"start": v(263.33, 210.52) * mm, "end": v(261.08, 210.52) * mm});
            skLineSegment(sketch, "E386", {"start": v(265.87, 207.98) * mm, "end": v(265.87, 205.73) * mm});
            skLineSegment(sketch, "E387", {"start": v(268.41, 210.52) * mm, "end": v(270.66, 210.52) * mm});
            skLineSegment(sketch, "E388", {"start": v(265.87, 213.06) * mm, "end": v(265.87, 215.3) * mm});
            skLineSegment(sketch, "E389", {"start": v(247.87, 210.52) * mm, "end": v(245.33, 210.52) * mm});
            skLineSegment(sketch, "E390", {"start": v(247.87, 210.52) * mm, "end": v(247.87, 207.98) * mm});
            skLineSegment(sketch, "E391", {"start": v(247.87, 210.52) * mm, "end": v(250.41, 210.52) * mm});
            skLineSegment(sketch, "E392", {"start": v(247.87, 210.52) * mm, "end": v(247.87, 213.06) * mm});
            skLineSegment(sketch, "E393", {"start": v(245.33, 210.52) * mm, "end": v(243.08, 210.52) * mm});
            skLineSegment(sketch, "E394", {"start": v(247.87, 207.98) * mm, "end": v(247.87, 205.73) * mm});
            skLineSegment(sketch, "E395", {"start": v(250.41, 210.52) * mm, "end": v(252.66, 210.52) * mm});
            skLineSegment(sketch, "E396", {"start": v(247.87, 213.06) * mm, "end": v(247.87, 215.3) * mm});
            skLineSegment(sketch, "E397", {"start": v(247.87, 234.52) * mm, "end": v(245.33, 234.52) * mm});
            skLineSegment(sketch, "E398", {"start": v(247.87, 234.52) * mm, "end": v(247.87, 231.98) * mm});
            skLineSegment(sketch, "E399", {"start": v(247.87, 234.52) * mm, "end": v(250.41, 234.52) * mm});
            skLineSegment(sketch, "E400", {"start": v(247.87, 234.52) * mm, "end": v(247.87, 237.06) * mm});
            skLineSegment(sketch, "E401", {"start": v(245.33, 234.52) * mm, "end": v(243.08, 234.52) * mm});
            skLineSegment(sketch, "E402", {"start": v(247.87, 231.98) * mm, "end": v(247.87, 229.73) * mm});
            skLineSegment(sketch, "E403", {"start": v(250.41, 234.52) * mm, "end": v(252.66, 234.52) * mm});
            skLineSegment(sketch, "E404", {"start": v(247.87, 237.06) * mm, "end": v(247.87, 239.3) * mm});
            skLineSegment(sketch, "E405", {"start": v(159.87, 210.52) * mm, "end": v(157.33, 210.52) * mm});
            skLineSegment(sketch, "E406", {"start": v(159.87, 210.52) * mm, "end": v(159.87, 207.98) * mm});
            skLineSegment(sketch, "E407", {"start": v(159.87, 210.52) * mm, "end": v(162.41, 210.52) * mm});
            skLineSegment(sketch, "E408", {"start": v(159.87, 210.52) * mm, "end": v(159.87, 213.06) * mm});
            skLineSegment(sketch, "E409", {"start": v(157.33, 210.52) * mm, "end": v(155.08, 210.52) * mm});
            skLineSegment(sketch, "E410", {"start": v(159.87, 207.98) * mm, "end": v(159.87, 205.73) * mm});
            skLineSegment(sketch, "E411", {"start": v(162.41, 210.52) * mm, "end": v(164.66, 210.52) * mm});
            skLineSegment(sketch, "E412", {"start": v(159.87, 213.06) * mm, "end": v(159.87, 215.3) * mm});
            skLineSegment(sketch, "E413", {"start": v(159.87, 234.52) * mm, "end": v(157.33, 234.52) * mm});
            skLineSegment(sketch, "E414", {"start": v(159.87, 234.52) * mm, "end": v(159.87, 231.98) * mm});
            skLineSegment(sketch, "E415", {"start": v(159.87, 234.52) * mm, "end": v(162.41, 234.52) * mm});
            skLineSegment(sketch, "E416", {"start": v(159.87, 234.52) * mm, "end": v(159.87, 237.06) * mm});
            skLineSegment(sketch, "E417", {"start": v(157.33, 234.52) * mm, "end": v(155.08, 234.52) * mm});
            skLineSegment(sketch, "E418", {"start": v(159.87, 231.98) * mm, "end": v(159.87, 229.73) * mm});
            skLineSegment(sketch, "E419", {"start": v(162.41, 234.52) * mm, "end": v(164.66, 234.52) * mm});
            skLineSegment(sketch, "E420", {"start": v(159.87, 237.06) * mm, "end": v(159.87, 239.3) * mm});
            skLineSegment(sketch, "E421", {"start": v(283.87, 234.52) * mm, "end": v(281.33, 234.52) * mm});
            skLineSegment(sketch, "E422", {"start": v(283.87, 234.52) * mm, "end": v(283.87, 231.98) * mm});
            skLineSegment(sketch, "E423", {"start": v(283.87, 234.52) * mm, "end": v(286.41, 234.52) * mm});
            skLineSegment(sketch, "E424", {"start": v(283.87, 234.52) * mm, "end": v(283.87, 237.06) * mm});
            skLineSegment(sketch, "E425", {"start": v(281.33, 234.52) * mm, "end": v(279.08, 234.52) * mm});
            skLineSegment(sketch, "E426", {"start": v(283.87, 231.98) * mm, "end": v(283.87, 229.73) * mm});
            skLineSegment(sketch, "E427", {"start": v(286.41, 234.52) * mm, "end": v(288.66, 234.52) * mm});
            skLineSegment(sketch, "E428", {"start": v(283.87, 237.06) * mm, "end": v(283.87, 239.3) * mm});
            skLineSegment(sketch, "E429", {"start": v(283.87, 210.52) * mm, "end": v(281.33, 210.52) * mm});
            skLineSegment(sketch, "E430", {"start": v(283.87, 210.52) * mm, "end": v(283.87, 207.98) * mm});
            skLineSegment(sketch, "E431", {"start": v(283.87, 210.52) * mm, "end": v(286.41, 210.52) * mm});
            skLineSegment(sketch, "E432", {"start": v(283.87, 210.52) * mm, "end": v(283.87, 213.06) * mm});
            skLineSegment(sketch, "E433", {"start": v(281.33, 210.52) * mm, "end": v(279.08, 210.52) * mm});
            skLineSegment(sketch, "E434", {"start": v(283.87, 207.98) * mm, "end": v(283.87, 205.73) * mm});
            skLineSegment(sketch, "E435", {"start": v(286.41, 210.52) * mm, "end": v(288.66, 210.52) * mm});
            skLineSegment(sketch, "E436", {"start": v(283.87, 213.06) * mm, "end": v(283.87, 215.3) * mm});
            skSolve(sketch);
        }
        {
            var Q0;
            Q0=makeQuery(id+"F0.imprint","IMPRINT",FACE,{"disambiguationData":[TD([[makeQuery(id+"F0.imprint","IMPRINT",EDGE,{"derivedFrom":sQuery(id+"F0.wireOp",EDGE,"E0")}),1.0]])]});
            extrude(context, id + "F1", {"entities" : qUnion([Q0]), "depth" : 3 * mm, "offsetDistance" : 25 * mm});
        }
    });
